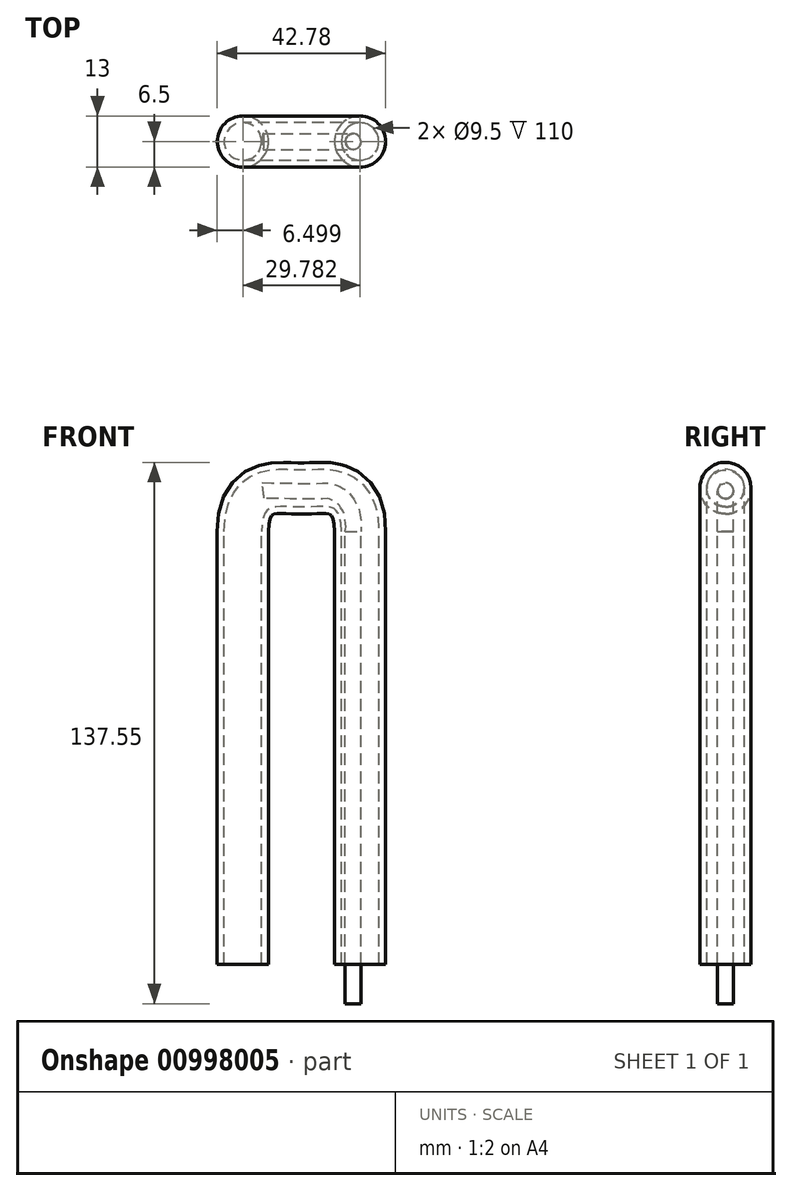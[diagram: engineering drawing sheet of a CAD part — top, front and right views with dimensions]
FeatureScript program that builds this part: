
annotation { "Feature Type Name" : "Feature", "Feature Type Description" : "" }
export const myFeature = defineFeature(function(context is Context, id is Id, definition is map)
    precondition{}
    {
        {
            var Q0;
            Q0=qCreatedBy(makeId("Front.planeOp"),FACE);
            var sketch = newSketch(context, id + "F0", { "sketchPlane" : qUnion([Q0])});
            skFitSpline(sketch, "E0", {"points": [v(-12, 0) * mm, v(0, 8) * mm, v(12, 0) * mm], "startDerivative": vector(0, 60) * mm, "endDerivative": vector(0, -60) * mm});
            skFitSpline(sketch, "E1", {"points": [v(-9.78, 10.61) * mm, v(0, 10.44) * mm, v(6.17, 10.48) * mm, v(7.44, 10.37) * mm, v(9.68, 9.38) * mm, v(10.89, 8.48) * mm, v(11.74, 7.27) * mm, v(12.9, 5.12) * mm, v(13.2, 3.28) * mm, v(13.42, 1.33) * mm, v(13.3, 0) * mm], "startDerivative": vector(42.98, -0.88) * mm, "endDerivative": vector(-2.7, -17.24) * mm});
            skSolve(sketch);
        }
        {
            var Q0;
            Q0=sQuery(id+"F0.wireOp",VERTEX,"E0.end");
            var Q1;
            Q1=sQuery(id+"F0.wireOp",EDGE,"E0");
            cPlane(context, id + "F1", {"entities" : qUnion([Q0, Q1]), "cplaneType" : CPlaneType.CURVE_POINT, "offset" : 25 * mm, "width" : 150 * mm, "height" : 150 * mm});
        }
        {
            var Q0;
            Q0=qCreatedBy(id+"F1.planeOp",FACE);
            var sketch = newSketch(context, id + "F2", { "sketchPlane" : qUnion([Q0])});
            skCircle(sketch, "E2", {"center": v(14.9, 0) * mm, "radius": 4.75 * mm});
            skCircle(sketch, "E3", {"center": v(14.9, 0) * mm, "radius": 6.5 * mm});
            skCircle(sketch, "E4", {"center": v(13.09, 0) * mm, "radius": 2 * mm});
            skSolve(sketch);
        }
        {
            var Q0;
            Q0=makeQuery(id+"F2.imprint","IMPRINT",FACE,{"disambiguationData":[TD([[makeQuery(id+"F2.imprint","IMPRINT",EDGE,{"derivedFrom":sQuery(id+"F2.wireOp",EDGE,"E2")}),-1.0]])]});
            var Q1;
            Q1=sQuery(id+"F0.wireOp",EDGE,"E0");
            sweep(context, id + "F3", {"profiles" : qUnion([Q0]), "path" : qUnion([Q1])});
        }
        {
            var Q0;
            Q0=makeQuery(id+"F3.opSweep","CAP_FACE",FACE,{"disambiguationData":[OSD([sQuery(id+"F0.wireOp",VERTEX,"E0.start"),sQuery(id+"F2.wireOp",EDGE,"E2"),sQuery(id+"F2.wireOp",EDGE,"E3")])],"isStart":false});
            var Q1;
            Q1=makeQuery(id+"F3.opSweep","CAP_FACE",FACE,{"disambiguationData":[OSD([sQuery(id+"F0.wireOp",VERTEX,"E0.end"),sQuery(id+"F2.wireOp",EDGE,"E2"),sQuery(id+"F2.wireOp",EDGE,"E3")])],"isStart":true});
            extrude(context, id + "F4", {"entities" : qUnion([Q0, Q1]), "operationType" : NewBodyOperationType.ADD, "depth" : 110 * mm, "offsetDistance" : 25 * mm});
        }
        {
            var Q0;
            Q0=makeQuery(id+"F2.imprint","IMPRINT",FACE,{"disambiguationData":[TD([[makeQuery(id+"F2.imprint","IMPRINT",EDGE,{"derivedFrom":sQuery(id+"F2.wireOp",EDGE,"E4")}),1.0]])]});
            var Q1;
            Q1=sQuery(id+"F0.wireOp",EDGE,"E1");
            sweep(context, id + "F5", {"profiles" : qUnion([Q0]), "path" : qUnion([Q1])});
        }
        {
            var Q0;
            Q0=makeQuery(id+"F2.imprint","IMPRINT",FACE,{"disambiguationData":[TD([[makeQuery(id+"F2.imprint","IMPRINT",EDGE,{"derivedFrom":sQuery(id+"F2.wireOp",EDGE,"E4")}),1.0]])]});
            extrude(context, id + "F6", {"entities" : qUnion([Q0]), "operationType" : NewBodyOperationType.ADD, "depth" : 120 * mm, "offsetDistance" : 25 * mm});
        }
    });
